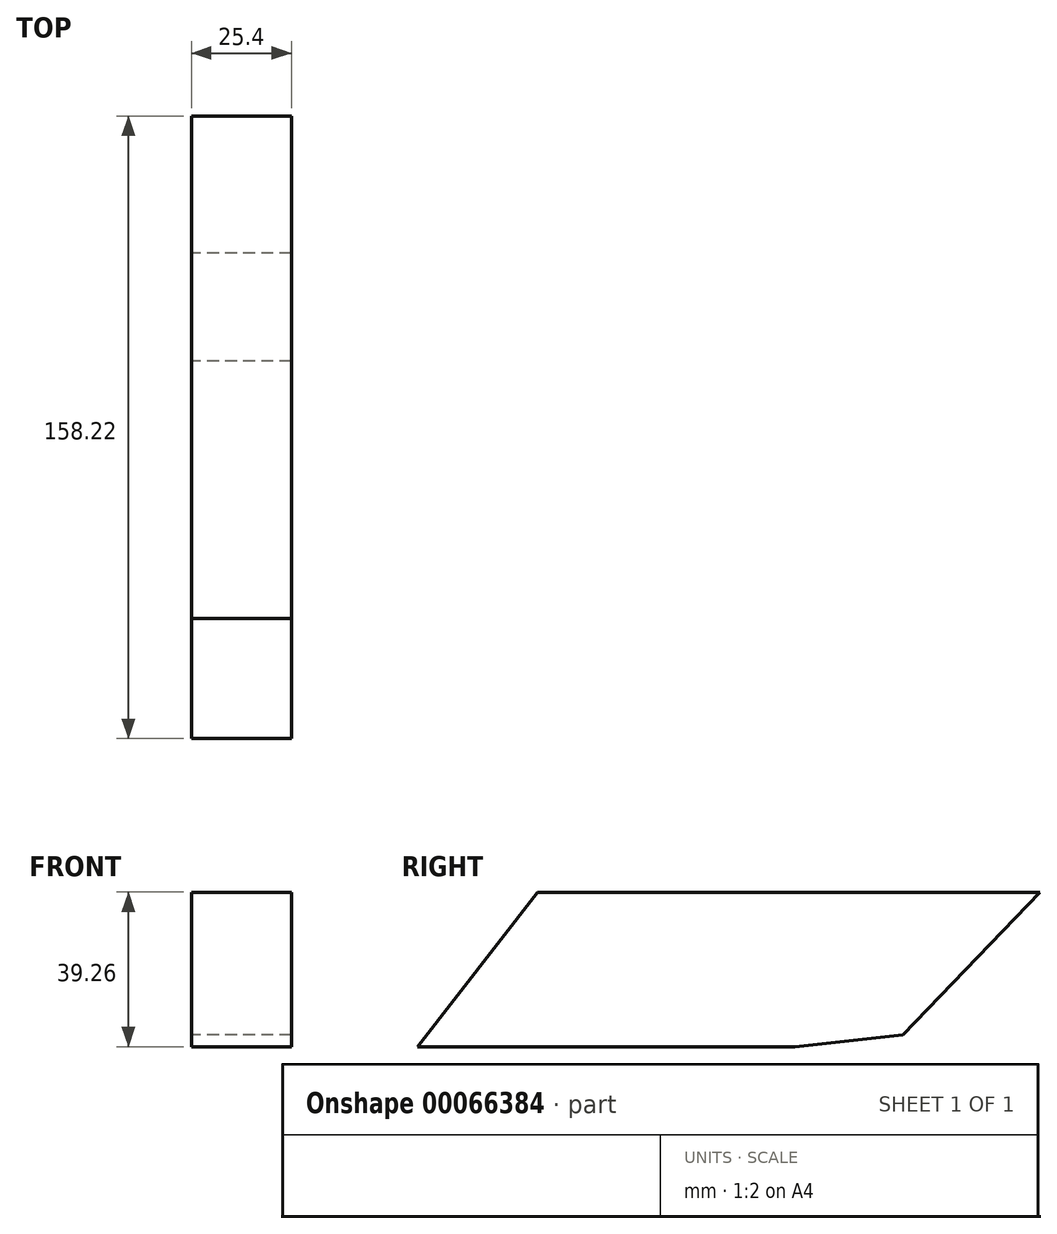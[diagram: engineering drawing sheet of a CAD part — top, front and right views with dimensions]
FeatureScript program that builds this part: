
annotation { "Feature Type Name" : "Feature", "Feature Type Description" : "" }
export const myFeature = defineFeature(function(context is Context, id is Id, definition is map)
    precondition{}
    {
        {
            var Q0;
            Q0=qCreatedBy(makeId("Front.planeOp"),FACE);
            var sketch = newSketch(context, id + "F0", { "sketchPlane" : qUnion([Q0])});
            skCircle(sketch, "E0", {"center": v(-21.94, 7.7) * mm, "radius": 74.54 * mm});
            skSolve(sketch);
        }
        {
            var Q0;
            Q0 = qSketchRegion(id + "F0", true);
            var Q1;
            Q1=sQuery(id+"F0.wireOp",EDGE,"E0");
            extrude(context, id + "F1", {"entities" : qUnion([Q0]), "bodyType" : ToolBodyType.SURFACE, "surfaceEntities" : qUnion([Q1]), "endBound" : BoundingType.SYMMETRIC, "depth" : 25.4 * mm});
        }
        {
            var Q0;
            Q0=qCreatedBy(makeId("Right.planeOp"),FACE);
            var sketch = newSketch(context, id + "F2", { "sketchPlane" : qUnion([Q0])});
            skLineSegment(sketch, "E1", {"start": v(-65.45, 39.26) * mm, "end": v(62.26, 39.26) * mm});
            skLineSegment(sketch, "E2", {"start": v(62.26, 39.26) * mm, "end": v(27.42, 3) * mm});
            skLineSegment(sketch, "E3", {"start": v(-65.45, 39.26) * mm, "end": v(-95.96, 0) * mm});
            skLineSegment(sketch, "E4", {"start": v(27.42, 3) * mm, "end": v(0, 0) * mm});
            skLineSegment(sketch, "E5", {"start": v(0, 0) * mm, "end": v(-95.96, 0) * mm});
            skSolve(sketch);
        }
        {
            var Q0;
            Q0 = qSketchRegion(id + "F2", true);
            extrude(context, id + "F3", {"entities" : qUnion([Q0]), "depth" : 25.4 * mm});
        }
    });
